# Revit family: Tub_Spout-Diverter-Grohe-13284002
name_source: partatom
category: Plumbing Fixtures
revit_build: Autodesk Revit 2018 (Build: 20170223_1515(x64)
units: mm (PartAtom-declared; Revit-internal decimal feet)

## family parameters
Cut with Voids When Loaded = No
Host = Face
OmniClass Number = 23.45.05.14.21.11
OmniClass Title = Bath/Shower Units
Part Type = Normal
Room Calculation Point = No
Round Connector Dimension = Use Diameter
Shared = Yes

## types (1)
- 13284002
    Assembly Code = D2090800
    Body Material = Metal-Grohe-002-Starlight Chrome
    CW Connection = Yes
    CWFU = 3
    Default Elevation = 0"
    Description = EUROSTYLE COSMOPOLITAN Tub Spout
    HW Connection = Yes
    HWFU = 3
    Height = 3 1/8"
    Installation Type = Wall Mounted
    Length = 6 11/16"
    Manufacturer = Grohe
    Material = Metal-Grohe-002-Starlight_Chrome
    Model = 13284002
    Price = Prices may vary. Please consult Manufacturer Representative for most up-to-date price list.
    Product Documentation Link = https://americanstandard.box.com
    Product Page URL = https://www.grohe.us
    Region = North America
    Tempered Water Connection Diameter = 1/2"
    URL = https://www.grohe.us
    Vent Connection = No
    WFU = 4
    Warranty Information = Lifetime Limited Warranty
    Waste Connection = No
    Width = 3 1/8"

## geometry (parser evidence)
native form markers: Sweep x3
no freeform markers — native parametric forms only
